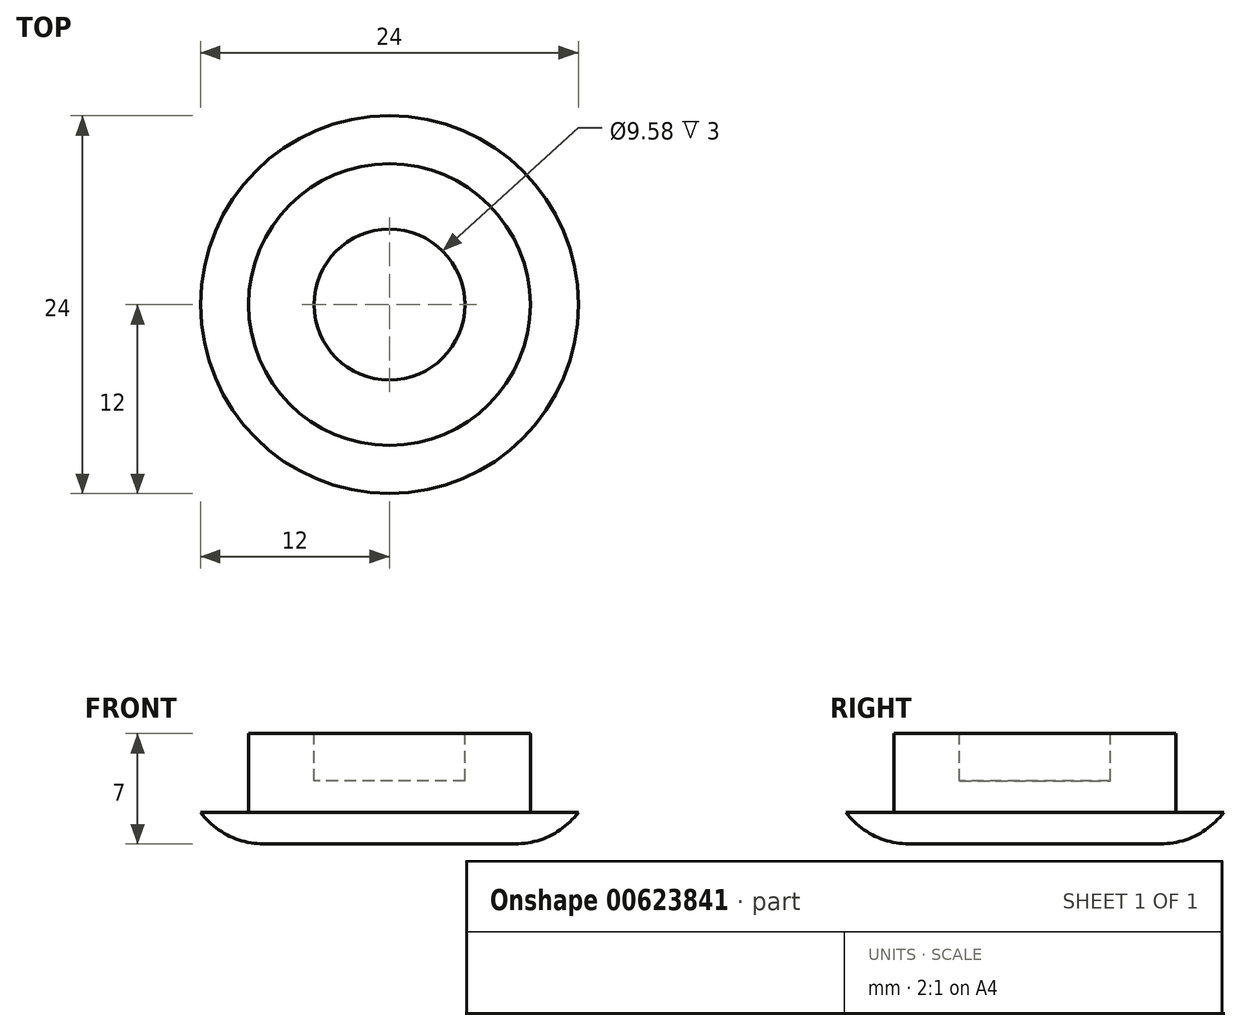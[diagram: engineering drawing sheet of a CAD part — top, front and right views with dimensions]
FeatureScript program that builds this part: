
annotation { "Feature Type Name" : "Feature", "Feature Type Description" : "" }
export const myFeature = defineFeature(function(context is Context, id is Id, definition is map)
    precondition{}
    {
        {
            var Q0;
            Q0=qCreatedBy(makeId("Top.planeOp"),FACE);
            var sketch = newSketch(context, id + "F0", { "sketchPlane" : qUnion([Q0])});
            skCircle(sketch, "E0", {"center": v(0, 0) * mm, "radius": 12 * mm});
            skSolve(sketch);
        }
        {
            var Q0;
            Q0 = qSketchRegion(id + "F0", true);
            extrude(context, id + "F1", {"entities" : qUnion([Q0]), "depth" : 2 * mm, "offsetDistance" : 25 * mm});
        }
        {
            var Q0;
            Q0=makeQuery(id+"F1.opExtrude","CAP_FACE",FACE,{"disambiguationData":[OSD([sQuery(id+"F0.wireOp",EDGE,"E0")])],"isStart":false});
            var sketch = newSketch(context, id + "F2", { "sketchPlane" : qUnion([Q0])});
            skCircle(sketch, "E1", {"center": v(0, 0) * mm, "radius": 8.95 * mm});
            skSolve(sketch);
        }
        {
            var Q0;
            Q0=makeQuery(id+"F2.imprint","IMPRINT",FACE,{"disambiguationData":[TD([[makeQuery(id+"F2.imprint","IMPRINT",EDGE,{"derivedFrom":sQuery(id+"F2.wireOp",EDGE,"E1")}),1.0]])]});
            extrude(context, id + "F3", {"entities" : qUnion([Q0]), "operationType" : NewBodyOperationType.ADD, "depth" : 5 * mm, "offsetDistance" : 25 * mm});
        }
        {
            var Q0;
            Q0=makeQuery(id+"F3.opExtrude","CAP_FACE",FACE,{"disambiguationData":[OSD([sQuery(id+"F2.wireOp",EDGE,"E1")])],"isStart":false});
            var sketch = newSketch(context, id + "F4", { "sketchPlane" : qUnion([Q0])});
            skCircle(sketch, "E2", {"center": v(0, 0) * mm, "radius": 4.8 * mm});
            skSolve(sketch);
        }
        {
            var Q0;
            Q0=makeQuery(id+"F4.imprint","IMPRINT",FACE,{"disambiguationData":[TD([[makeQuery(id+"F4.imprint","IMPRINT",EDGE,{"derivedFrom":sQuery(id+"F4.wireOp",EDGE,"E2")}),1.0]])]});
            extrude(context, id + "F5", {"entities" : qUnion([Q0]), "operationType" : NewBodyOperationType.REMOVE, "oppositeDirection" : true, "depth" : 3 * mm, "offsetDistance" : 25 * mm});
        }
        {
            var Q0;
            Q0=makeQuery(id+"F1.opExtrude","CAP_EDGE",EDGE,{"disambiguationData":[OSD([sQuery(id+"F0.wireOp",EDGE,"E0")])],"isStart":true});
            fillet(context, id + "F6", {"entities" : qUnion([Q0]), "radius" : 5 * mm, "tangentPropagation" : true, "allowEdgeOverflow" : false});
        }
    });
